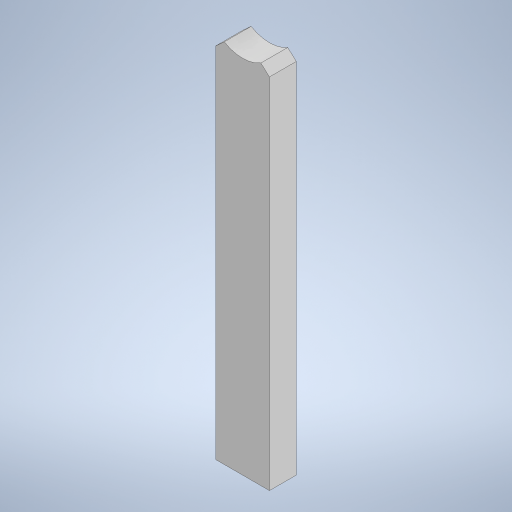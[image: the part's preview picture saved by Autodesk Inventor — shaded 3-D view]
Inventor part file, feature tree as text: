
AUTODESK INVENTOR PART (.ipt)
format: ipt  version: 2023 (Build 270158000, 158)  size: 234,496 bytes
history: native  units: mm
features: extrude x1, sketch x1
ambient origin geometry x8: Origin, YZ Plane, XZ Plane, XY Plane, X Axis, Y Axis, Z Axis, Center Point
bodies: Solid1 (feature_tree)
feature tree (2):
  extrude  "Extrusion1"  Depth=15.0mm
  sketch  "Sketch2"  dims[d3=24.03232mm d4=16.648713mm d5=4.353348mm d15=200.0mm d16=200.0mm d17=15.0mm d18=0.0mm]
